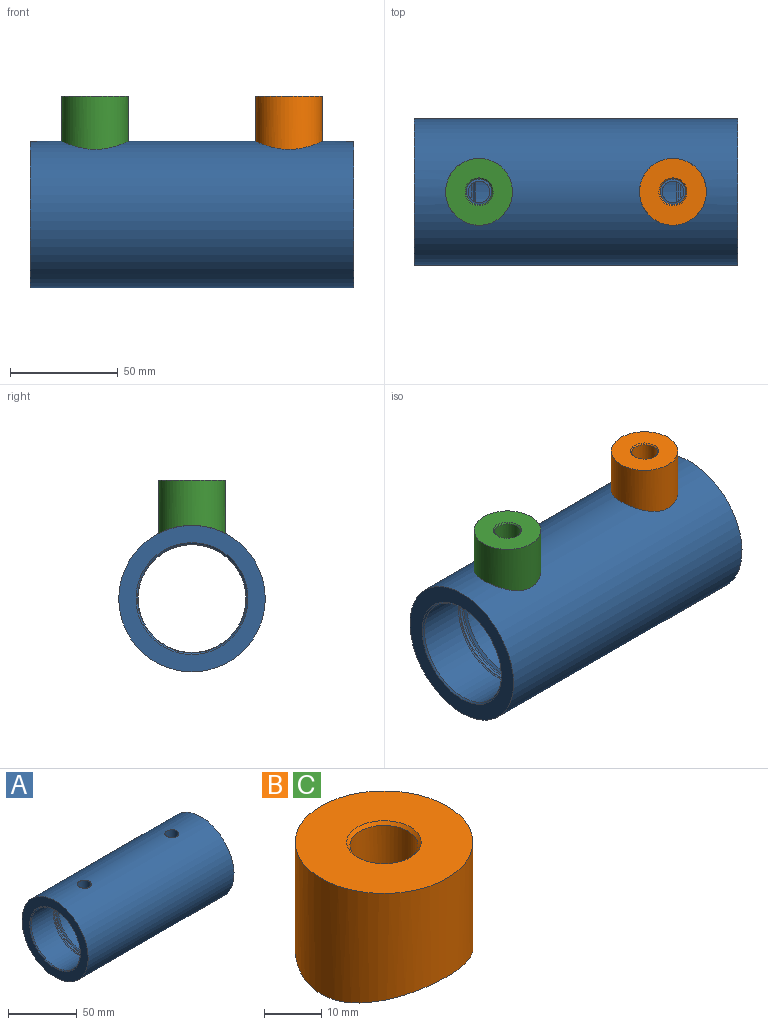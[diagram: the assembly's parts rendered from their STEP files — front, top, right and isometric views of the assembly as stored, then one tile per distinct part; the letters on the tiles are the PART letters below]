
ASSEMBLY  parts=3 mates=3
PART A: 20 faces, bbox 150x68x68 mm
  f0: cylinder r=25mm len=93.4mm, axis (-1,0,0), area 14558.7mm2, adj f2,f6,f18,f19
  f1: cylinder r=34mm len=150mm, axis (1,0,0), area 31887.5mm2, adj f10,f11,f18,f19
  f2: cone r=25mm half-angle=45deg, axis (-1,0,0), area 215.5mm2, adj f0,f4,f19
  f3: cylinder r=26.3mm len=52.6mm, axis (1,0,0), area 210.3mm2, adj f4,f5,f19
  f4: torus R=25.3mm, axis (1,0,0), area 123.1mm2, adj f2,f3,f19
  f5: torus R=25.3mm, axis (1,0,0), area 85.8mm2, adj f3,f14,f19
  f6: cone r=25mm half-angle=45deg, axis (1,0,0), area 215.5mm2, adj f0,f8,f18
  f7: cylinder r=26.3mm len=52.6mm, axis (-1,0,0), area 210.3mm2, adj f8,f9,f18
  f8: torus R=25.3mm, axis (1,0,0), area 123.1mm2, adj f6,f7,f18
  f9: torus R=25.3mm, axis (1,0,0), area 85.8mm2, adj f7,f17,f18
  f10: plane 68x68mm, normal (-1,0,0), area 1508mm2, adj f1,f13
  f11: plane 68x68mm, normal (1,0,0), area 1508mm2, adj f1,f16
  f12: cylinder r=25.25mm len=50.5mm, axis (-1,0,0), area 3558.7mm2, adj f13,f14
  f13: cone r=25.25mm half-angle=45deg, axis (-1,0,0), area 170.8mm2, adj f10,f12
  f14: cone r=26.3mm half-angle=30deg, axis (1,0,0), area 295.9mm2, adj f5,f12
  f15: cylinder r=25.25mm len=50.5mm, axis (1,0,0), area 3558.7mm2, adj f16,f17
  f16: cone r=25.25mm half-angle=45deg, axis (1,0,0), area 170.8mm2, adj f11,f15
  f17: cone r=26.3mm half-angle=30deg, axis (-1,0,0), area 295.9mm2, adj f9,f15
  f18: cylinder r=5mm len=10mm, axis (0,0,-1), area 271mm2, adj f0,f1,f6,f7,f8,f9
  f19: cylinder r=5mm len=10mm, axis (0,0,-1), area 270.9mm2, adj f0,f1,f2,f3,f4,f5
PART B: 5 faces, bbox 31x31x24.7 mm
  f0: cylinder r=15.5mm len=31mm, axis (0,0,-1), area 2224.7mm2, adj f2,f4
  f1: cylinder r=5.95mm len=20.9mm, axis (0,0,1), area 771.9mm2, adj f3,f4
  f2: plane 31x31mm, normal (0,0,1), area 622mm2, adj f0,f3
  f3: cone r=5.95mm half-angle=41deg, axis (0,0,1), area 32.6mm2, adj f1,f2
  f4: cylinder r=34mm len=31mm, axis (0,1,0), area 663.8mm2, adj f0,f1
PART C: same geometry as B
PLACE A at identity fixed
PLACE B rot(axis=(0,0,-1),90deg) t=(45,0,30)mm
PLACE C rot(axis=(0,0,-1),90deg) t=(-45,0,30)mm
MATE cylindrical A.f0 <-> C.f4  axis (1,0,0) through (0,0,0)mm
MATE slider C.f0 <-> A.f19  axis (0,0,1) through (-45,0,43.86)mm
MATE cylindrical B.f4 <-> A.f0  axis (1,0,0) through (45,0,0)mm
